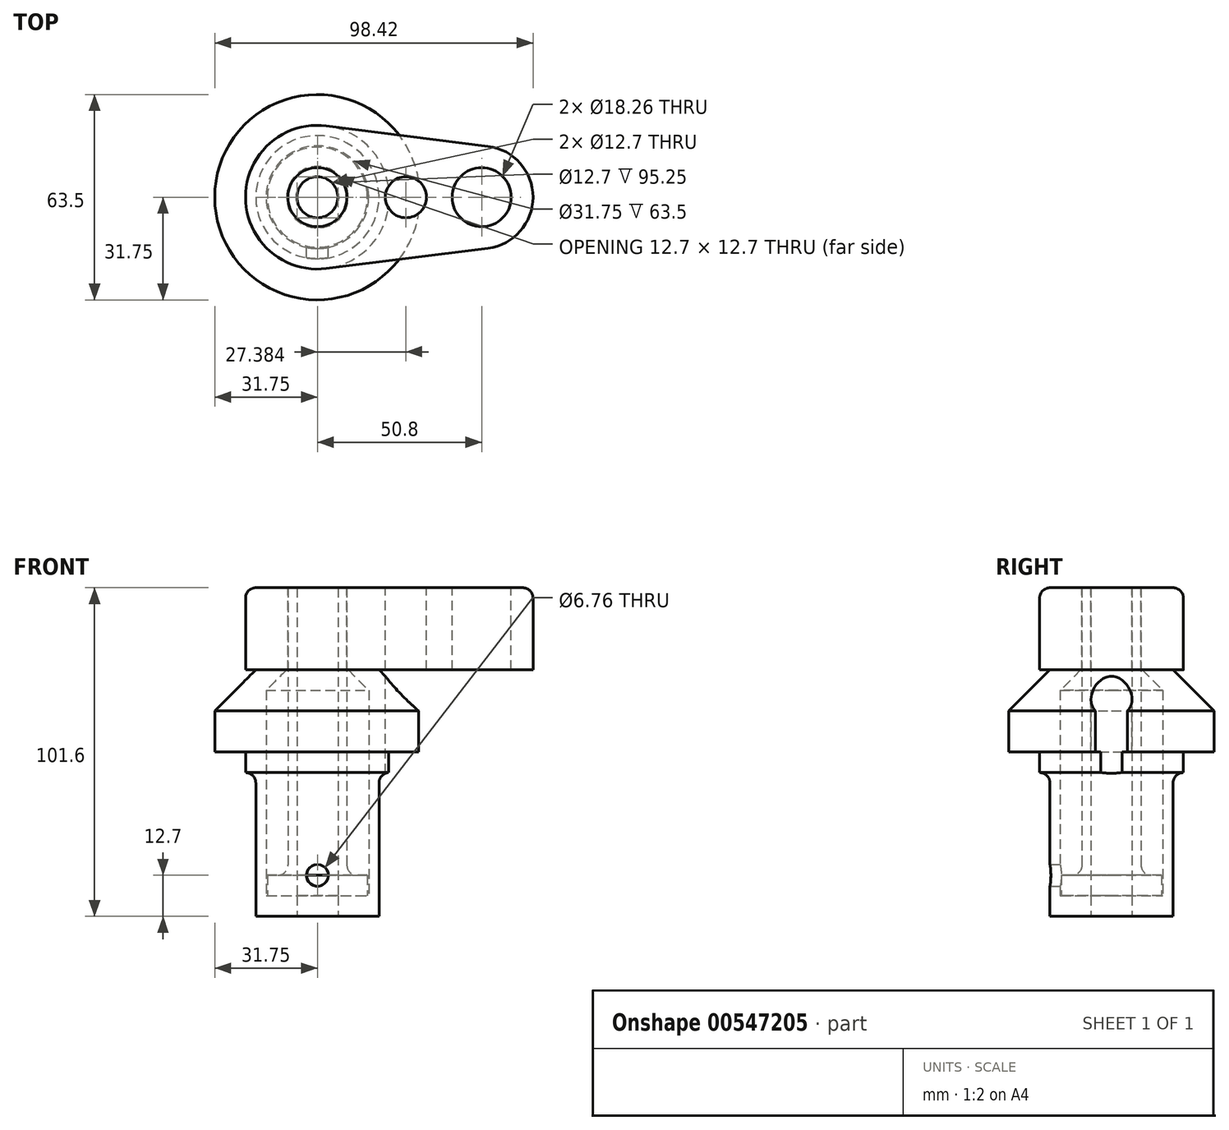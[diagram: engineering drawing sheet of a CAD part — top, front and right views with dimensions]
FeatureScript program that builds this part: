
annotation { "Feature Type Name" : "Feature", "Feature Type Description" : "" }
export const myFeature = defineFeature(function(context is Context, id is Id, definition is map)
    precondition{}
    {
        {
            var Q0;
            Q0=qCreatedBy(makeId("Front.planeOp"),FACE);
            var sketch = newSketch(context, id + "F0", { "sketchPlane" : qUnion([Q0])});
            skLineSegment(sketch, "E0", {"start": v(0, 0) * mm, "end": v(0, 76.2) * mm});
            skLineSegment(sketch, "E1", {"start": v(0, 76.2) * mm, "end": v(19.05, 76.2) * mm});
            skLineSegment(sketch, "E2", {"start": v(19.05, 76.2) * mm, "end": v(31.75, 63.5) * mm});
            skLineSegment(sketch, "E3", {"start": v(31.75, 63.5) * mm, "end": v(31.75, 50.8) * mm});
            skLineSegment(sketch, "E4", {"start": v(31.75, 50.8) * mm, "end": v(22.23, 50.8) * mm});
            skLineSegment(sketch, "E5", {"start": v(22.23, 50.8) * mm, "end": v(22.23, 44.45) * mm});
            skLineSegment(sketch, "E6", {"start": v(22.23, 44.45) * mm, "end": v(19.05, 44.45) * mm});
            skLineSegment(sketch, "E7", {"start": v(19.05, 44.45) * mm, "end": v(19.05, 0) * mm});
            skLineSegment(sketch, "E8", {"start": v(19.05, 0) * mm, "end": v(0, 0) * mm});
            skLineSegment(sketch, "E9", {"start": v(9.53, 76.2) * mm, "end": v(15.88, 69.85) * mm});
            skLineSegment(sketch, "E10", {"start": v(15.88, 69.85) * mm, "end": v(15.88, 6.35) * mm});
            skLineSegment(sketch, "E11", {"start": v(15.88, 6.35) * mm, "end": v(0, 6.35) * mm});
            skLineSegment(sketch, "E12", {"start": v(0, 76.2) * mm, "end": v(0, 93.83) * mm, "construction": true});
            skLineSegment(sketch, "E13", {"start": v(0, 76.2) * mm, "end": v(0, 101.6) * mm});
            skLineSegment(sketch, "E14", {"start": v(0, 101.6) * mm, "end": v(9.13, 101.6) * mm});
            skLineSegment(sketch, "E15", {"start": v(9.13, 101.6) * mm, "end": v(9.13, 12.7) * mm});
            skLineSegment(sketch, "E16", {"start": v(9.13, 12.7) * mm, "end": v(15.48, 12.7) * mm});
            skLineSegment(sketch, "E17", {"start": v(15.48, 12.7) * mm, "end": v(15.48, 6.35) * mm});
            skSolve(sketch);
        }
        {
            var Q0;
            {var subQ4=sQuery(id+"F0.wireOp",EDGE,"E2");Q0=makeQuery(id+"F0.imprint","IMPRINT",FACE,{"disambiguationData":[TD([[makeQuery(id+"F0.imprint","IMPRINT",EDGE,{"derivedFrom":subQ4}),-1.0]])]});}
            var Q1;
            Q1=sQuery(id+"F0.wireOp",EDGE,"E0");
            revolve(context, id + "F1", {"entities" : qUnion([Q0]), "axis" : qUnion([Q1]), "revolveType" : RevolveType.FULL});
        }
        {
            var Q0;
            {var subQ0=sQuery(id+"F0.wireOp",EDGE,"E13");Q0=makeQuery(id+"F0.imprint","IMPRINT",FACE,{"disambiguationData":[TD([[makeQuery(id+"F0.imprint","IMPRINT",EDGE,{"derivedFrom":subQ0}),-1.0]])]});}
            var Q1;
            {var subQ0=sQuery(id+"F0.wireOp",EDGE,"E16");Q1=makeQuery(id+"F0.imprint","IMPRINT",FACE,{"disambiguationData":[TD([[makeQuery(id+"F0.imprint","IMPRINT",EDGE,{"derivedFrom":subQ0}),-1.0]])]});}
            var Q2;
            Q2=sQuery(id+"F0.wireOp",EDGE,"E13");
            revolve(context, id + "F2", {"entities" : qUnion([Q0, Q1]), "axis" : qUnion([Q2]), "revolveType" : RevolveType.FULL});
        }
        {
            var Q0;
            Q0=makeQuery(id+"F2.opRevolve","SWEPT_FACE",FACE,{"disambiguationData":[OSD([sQuery(id+"F0.wireOp",EDGE,"E14")])]});
            var sketch = newSketch(context, id + "F3", { "sketchPlane" : qUnion([Q0])});
            skCircle(sketch, "E18", {"center": v(0, 0) * mm, "radius": 22.23 * mm});
            skCircle(sketch, "E19", {"center": v(50.8, 0) * mm, "radius": 15.88 * mm});
            skLineSegment(sketch, "E20", {"start": v(2.78, 22.05) * mm, "end": v(52.78, 15.75) * mm});
            skLineSegment(sketch, "E21", {"start": v(52.78, -15.75) * mm, "end": v(2.78, -22.05) * mm});
            skCircle(sketch, "E22.0", {"center": v(0, 0) * mm, "radius": 9.13 * mm});
            skCircle(sketch, "E23", {"center": v(50.8, 0) * mm, "radius": 9.13 * mm});
            skSolve(sketch);
        }
        {
            var Q0;
            Q0 = qSketchRegion(id + "F3", true);
            var Q1;
            Q1=makeQuery(id+"F1.opRevolve","SWEPT_FACE",FACE,{"disambiguationData":[OSD([sQuery(id+"F0.wireOp",EDGE,"E1")])]});
            extrude(context, id + "F4", {"entities" : qUnion([Q0]), "oppositeDirection" : true, "depth" : 25.4 * mm, "endBoundEntityFace" : qUnion([Q1]), "offsetDistance" : 1 / 406.4 * mm});
        }
        {
            var Q0;
            Q0=qCreatedBy(makeId("Front.planeOp"),FACE);
            var sketch = newSketch(context, id + "F5", { "sketchPlane" : qUnion([Q0])});
            skPoint(sketch, "E24", {"position": v(0, 12.7) * mm});
            skSolve(sketch);
        }
        {
            var Q0;
            Q0=sQuery(id+"F5.wireOp",VERTEX,"E24");
            var Q1;
            Q1=makeQuery(id+"F1.opRevolve","SWEPT_BODY",BODY,{"disambiguationData":[OSD([sQuery(id+"F0.wireOp",EDGE,"E0"),sQuery(id+"F0.wireOp",EDGE,"E1"),sQuery(id+"F0.wireOp",EDGE,"E2"),sQuery(id+"F0.wireOp",EDGE,"E3"),sQuery(id+"F0.wireOp",EDGE,"E4"),sQuery(id+"F0.wireOp",EDGE,"E5"),sQuery(id+"F0.wireOp",EDGE,"E6"),sQuery(id+"F0.wireOp",EDGE,"E7"),sQuery(id+"F0.wireOp",EDGE,"E8"),sQuery(id+"F0.wireOp",EDGE,"E9"),sQuery(id+"F0.wireOp",EDGE,"E10"),sQuery(id+"F0.wireOp",EDGE,"E11")])]});
            hole(context, id + "F6", {"style" : HoleStyle.SIMPLE, "endStyle" : HoleEndStyle.THROUGH, "oppositeDirection" : true, "standardTappedOrClearance" : lookupTablePath({ "standard" : "ANSI", "fit" : "Normal (ASME)", "size" : "1/4", "type" : "Clearance" }), "standardBlindInLast" : lookupTablePath({ "fit" : "Free", "standard" : "ANSI", "size" : "1/4", "type" : "Clearance" }), "holeDiameter" : 6.76 * mm, "tappedDepth" : 14.3 * mm, "tapClearance" : 3, "locations" : qUnion([Q0]), "scope" : qUnion([Q1])});
        }
        {
            var Q0;
            Q0=makeQuery(id+"F4.opExtrude","CAP_EDGE",EDGE,{"disambiguationData":[OSD([sQuery(id+"F3.wireOp",EDGE,"E18")])],"isStart":true});
            var Q1;
            Q1=makeQuery(id+"F1.opRevolve","SWEPT_EDGE",EDGE,{"disambiguationData":[OSD([sQuery(id+"F0.wireOp",EDGE,"E6"),sQuery(id+"F0.wireOp",EDGE,"E7")])]});
            var Q2;
            Q2=makeQuery(id+"F2.opRevolve","SWEPT_EDGE",EDGE,{"disambiguationData":[OSD([sQuery(id+"F0.wireOp",EDGE,"E15"),sQuery(id+"F0.wireOp",EDGE,"E16")])]});
            fillet(context, id + "F7", {"entities" : qUnion([Q0, Q1, Q2]), "radius" : 3.17 * mm, "tangentPropagation" : true, "allowEdgeOverflow" : false});
        }
        {
            var Q0;
            Q0=makeQuery(id+"F1.opRevolve","SWEPT_FACE",FACE,{"disambiguationData":[OSD([sQuery(id+"F0.wireOp",EDGE,"E8")])]});
            var sketch = newSketch(context, id + "F8", { "sketchPlane" : qUnion([Q0])});
            skCircle(sketch, "E25", {"center": v(0, 0) * mm, "radius": 6.35 * mm});
            skSolve(sketch);
        }
        {
            var Q0;
            Q0 = qSketchRegion(id + "F8", true);
            extrude(context, id + "F9", {"entities" : qUnion([Q0]), "operationType" : NewBodyOperationType.REMOVE, "endBound" : BoundingType.THROUGH_ALL, "oppositeDirection" : true, "depth" : 25.4 * mm, "offsetDistance" : 25.4 * mm});
        }
        {
            var Q0;
            Q0=makeQuery(id+"F4.opExtrude","CAP_FACE",FACE,{"disambiguationData":[OSD([sQuery(id+"F3.wireOp",EDGE,"E18"),sQuery(id+"F3.wireOp",EDGE,"E19"),sQuery(id+"F3.wireOp",EDGE,"E20"),sQuery(id+"F3.wireOp",EDGE,"E21"),sQuery(id+"F3.wireOp",EDGE,"E22.0"),sQuery(id+"F3.wireOp",EDGE,"E23")])],"isStart":true});
            var sketch = newSketch(context, id + "F10", { "sketchPlane" : qUnion([Q0])});
            skCircle(sketch, "E26", {"center": v(27.38, 0) * mm, "radius": 6.35 * mm});
            skPoint(sketch, "E26.centerSnap0", {"position": v(27.38, 15.75) * mm});
            skSolve(sketch);
        }
        {
            var Q0;
            Q0 = qSketchRegion(id + "F10", true);
            extrude(context, id + "F11", {"entities" : qUnion([Q0]), "operationType" : NewBodyOperationType.REMOVE, "endBound" : BoundingType.THROUGH_ALL, "oppositeDirection" : true, "depth" : 25.4 * mm, "offsetDistance" : 25.4 * mm});
        }
    });
